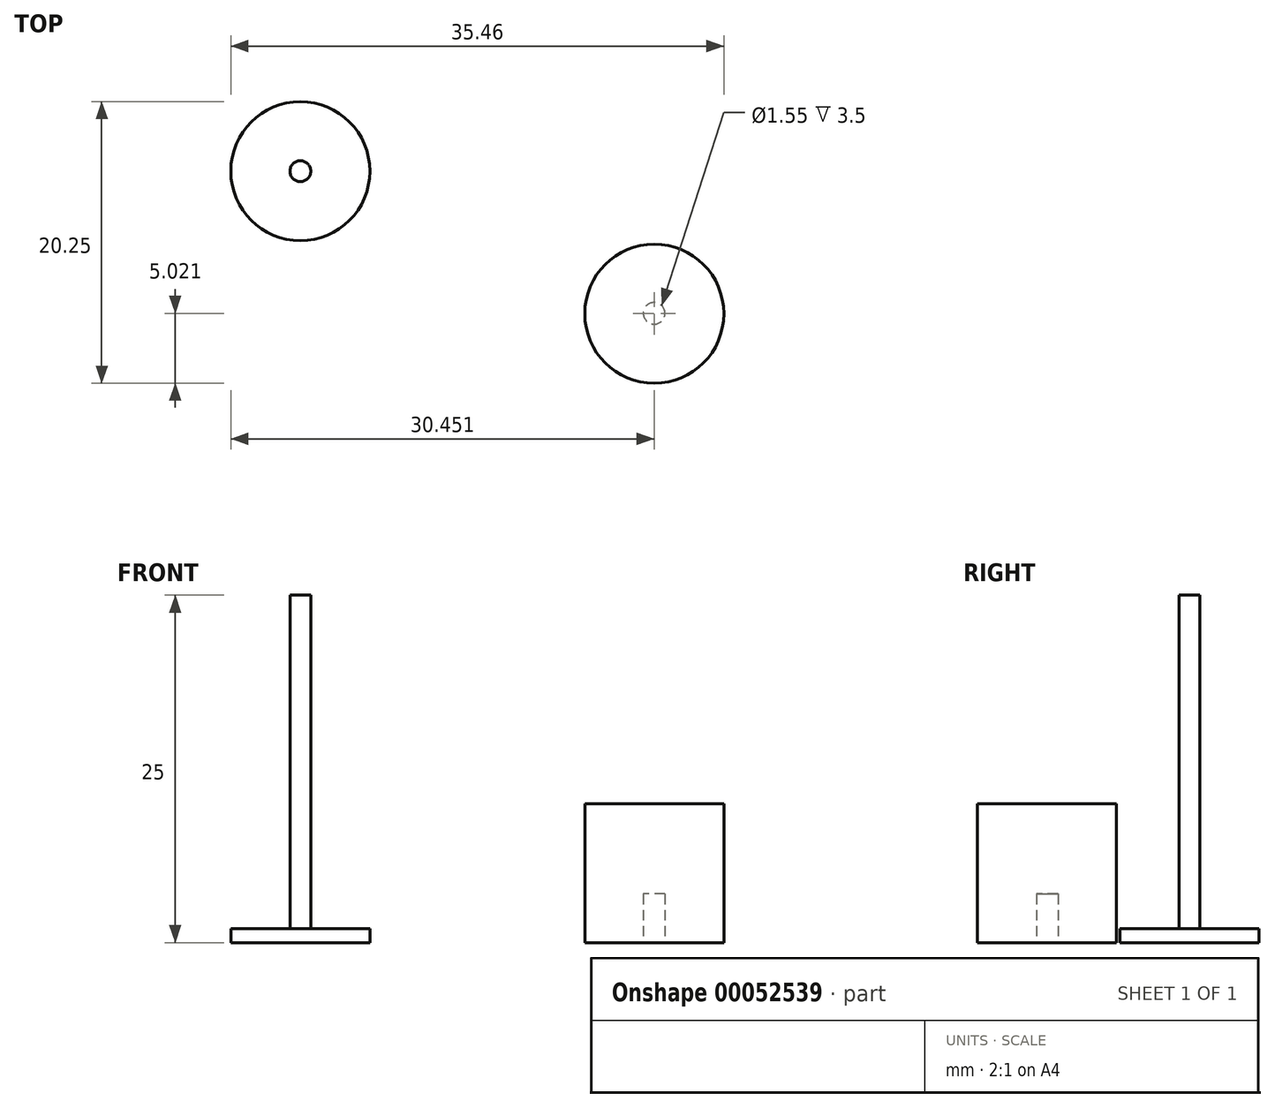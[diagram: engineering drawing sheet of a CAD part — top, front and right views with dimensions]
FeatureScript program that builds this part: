
annotation { "Feature Type Name" : "Feature", "Feature Type Description" : "" }
export const myFeature = defineFeature(function(context is Context, id is Id, definition is map)
    precondition{}
    {
        {
            var Q0;
            Q0=qCreatedBy(makeId("Top.planeOp"),FACE);
            var sketch = newSketch(context, id + "F0", { "sketchPlane" : qUnion([Q0])});
            skCircle(sketch, "E0", {"center": v(0, 0) * mm, "radius": 5 * mm});
            skCircle(sketch, "E1", {"center": v(0, 0) * mm, "radius": 0.75 * mm});
            skSolve(sketch);
        }
        {
            var Q0;
            Q0=makeQuery(id+"F0.imprint","IMPRINT",FACE,{"disambiguationData":[TD([[makeQuery(id+"F0.imprint","IMPRINT",EDGE,{"derivedFrom":sQuery(id+"F0.wireOp",EDGE,"E0")}),1.0]])]});
            extrude(context, id + "F1", {"entities" : qUnion([Q0]), "depth" : 1 * mm});
        }
        {
            var Q0;
            Q0=qCreatedBy(makeId("Top.planeOp"),FACE);
            var sketch = newSketch(context, id + "F2", { "sketchPlane" : qUnion([Q0])});
            skCircle(sketch, "E2", {"center": v(0, 0) * mm, "radius": 0.75 * mm});
            skSolve(sketch);
        }
        {
            var Q0;
            Q0=makeQuery(id+"F2.imprint","IMPRINT",FACE,{"disambiguationData":[TD([[makeQuery(id+"F2.imprint","IMPRINT",EDGE,{"derivedFrom":sQuery(id+"F2.wireOp",EDGE,"E2")}),1.0]])]});
            extrude(context, id + "F3", {"entities" : qUnion([Q0]), "operationType" : NewBodyOperationType.ADD, "depth" : 25 * mm});
        }
        {
            var Q0;
            Q0=qCreatedBy(makeId("Top.planeOp"),FACE);
            var sketch = newSketch(context, id + "F4", { "sketchPlane" : qUnion([Q0])});
            skCircle(sketch, "E3", {"center": v(25.46, -10.25) * mm, "radius": 5 * mm});
            skSolve(sketch);
        }
        {
            var Q0;
            Q0=makeQuery(id+"F4.imprint","IMPRINT",FACE,{"disambiguationData":[TD([[makeQuery(id+"F4.imprint","IMPRINT",EDGE,{"derivedFrom":sQuery(id+"F4.wireOp",EDGE,"E3")}),1.0]])]});
            var sketch = newSketch(context, id + "F5", { "sketchPlane" : qUnion([Q0])});
            skCircle(sketch, "E4", {"center": v(25.45, -10.23) * mm, "radius": 0.78 * mm});
            skSolve(sketch);
        }
        {
            var Q0;
            Q0 = qSketchRegion(id + "F4", true);
            extrude(context, id + "F6", {"entities" : qUnion([Q0]), "depth" : 10 * mm});
        }
        {
            var Q0;
            Q0 = qSketchRegion(id + "F5", true);
            extrude(context, id + "F7", {"entities" : qUnion([Q0]), "operationType" : NewBodyOperationType.REMOVE, "depth" : 3.5 * mm});
        }
    });
